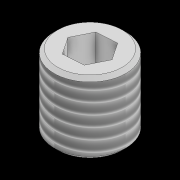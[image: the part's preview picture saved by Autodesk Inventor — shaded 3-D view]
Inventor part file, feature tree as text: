
AUTODESK INVENTOR PART (.ipt)
format: ipt  version: 2021 (Build 250183000, 183)  size: 118,272 bytes
history: native  units: mm
features: extrude x2, sketch x2, thread x1, chamfer x1
ambient origin geometry x8: Origin, YZ Plane, XZ Plane, XY Plane, X Axis, Y Axis, Z Axis, Center Point
bodies: Solid1 (feature_tree)
feature tree (6):
  extrude  "Extrusion1"  Depth=5.0mm
  extrude  "Extrusion2"  Depth=5.5mm TaperAngle=0.0deg
  thread  "Thread1"  [1 undecoded]
  chamfer  "Chamfer1"  Distance=0.5mm Angle=45.0deg
  sketch  "Sketch1"  dims[d0=10.0mm d1=0.0mm d2=5.0mm]
  sketch  "Sketch2"  dims[d3=10.0mm d4=5.5mm d5=0.0mm d6=10.0mm d7=0.0mm d8=0.5mm d9=2.0mm d10=45.0deg]
note: 1 required parameter value undecoded (feature->parameter linkage not recoverable at this tier; creation-order binding heuristic only, values carry confidence <= 0.55)
